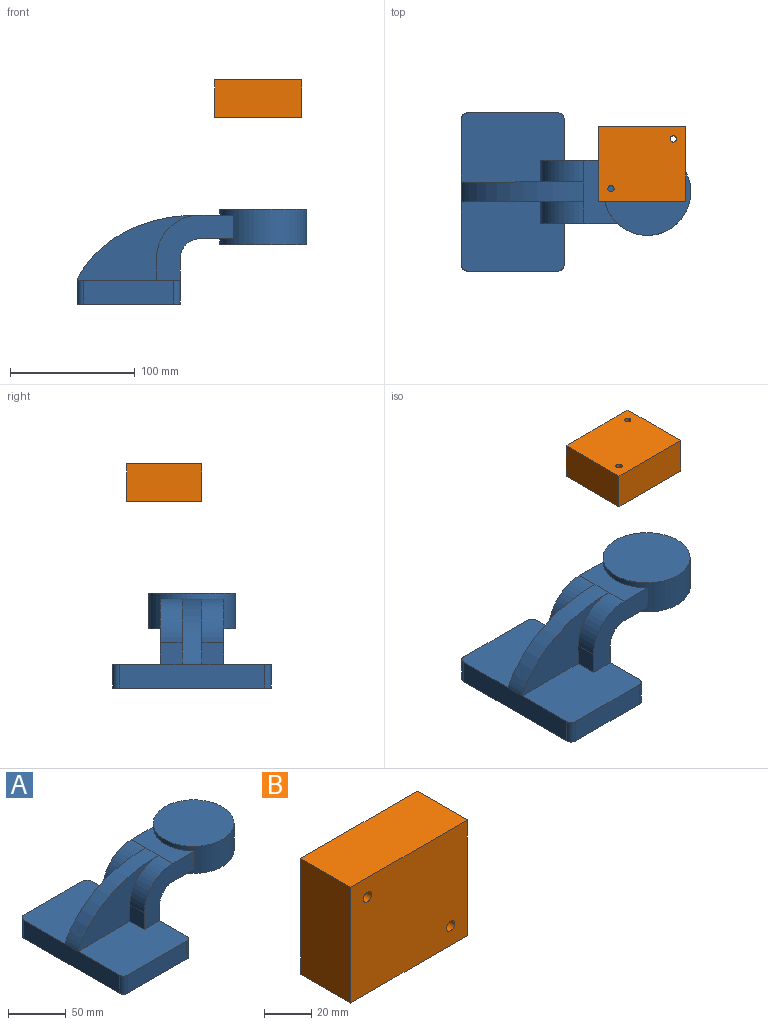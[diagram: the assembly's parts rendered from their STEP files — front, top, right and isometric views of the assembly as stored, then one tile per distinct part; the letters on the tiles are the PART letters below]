
ASSEMBLY  parts=2 mates=1
PART A: 26 faces, bbox 184.2x127x76.2 mm
  f0: plane 61.75x52.4mm, normal (0,-1,0), area 1604.1mm2, adj f5,f8,f11,f12,f13,f14,f15,f19
  f1: plane 61.75x52.4mm, normal (0,1,0), area 1604.1mm2, adj f2,f3,f4,f8,f11,f14,f15,f19
  f2: plane 82.55x55.56mm, normal (0,0,1), area 4242.9mm2, adj f1,f4,f6,f8,f10,f18,f22,f23
  f3: cylinder r=34.92mm len=34.93mm, axis (0,1,0), area 958mm2, adj f1,f4,f11,f18
  f4: plane 17.48x17.46mm, normal (-1,0,0), area 305.2mm2, adj f1,f2,f3,f18
  f5: plane 82.55x55.56mm, normal (0,0,1), area 4242.9mm2, adj f0,f6,f8,f9,f13,f17,f24,f25
  f6: plane 116.84x19.05mm, normal (-1,0,0), area 2225.8mm2, adj f2,f5,f7,f16,f22,f24
  f7: plane 127x82.55mm, normal (0,0,-1), area 10461.7mm2, adj f6,f8,f9,f10,f22,f23,f24,f25
  f8: plane 116.84x36.53mm, normal (1,0,0), area 3113.5mm2, adj f0,f1,f2,f5,f7,f14,f23,f25
  f9: plane 72.39x19.05mm, normal (0,-1,0), area 1379mm2, adj f5,f7,f24,f25
  f10: plane 72.39x19.05mm, normal (0,1,0), area 1379mm2, adj f2,f7,f22,f23
  f11: plane 50.8x26.83mm, normal (0,0,1), area 978.5mm2, adj f0,f1,f3,f12,f16,f19
  f12: cylinder r=34.92mm len=34.93mm, axis (0,1,0), area 958mm2, adj f0,f11,f13,f17
  f13: plane 17.48x17.46mm, normal (-1,0,0), area 305.2mm2, adj f0,f5,f12,f17
  f14: cylinder r=15.88mm len=50.8mm, axis (0,1,0), area 1266.8mm2, adj f0,f1,f8,f15
  f15: plane 50.8x26.83mm, normal (0,0,-1), area 978.5mm2, adj f0,f1,f14,f19
  f16: extruded ~98.43x52.4mm, area 1872.6mm2, adj f6,f11,f17,f18
  f17: plane 98.43x52.43mm, normal (0,-1,0), area 2250.7mm2, adj f5,f12,f13,f16
  f18: plane 98.43x52.43mm, normal (0,1,0), area 2250.7mm2, adj f2,f3,f4,f16
  f19: cylinder r=34.92mm len=69.85mm, axis (0,0,-1), area 5186.9mm2, adj f0,f1,f11,f15,f20,f21
  f20: plane 69.85x69.85mm, normal (0,0,-1), area 3832mm2, adj f19
  f21: plane 69.85x69.85mm, normal (0,0,1), area 3832mm2, adj f19
  f22: cylinder r=5.08mm len=19.05mm, axis (0,0,-1), area 152mm2, adj f2,f6,f7,f10
  f23: cylinder r=5.08mm len=19.05mm, axis (0,0,1), area 152mm2, adj f2,f7,f8,f10
  f24: cylinder r=5.08mm len=19.05mm, axis (0,0,1), area 152mm2, adj f5,f6,f7,f9
  f25: cylinder r=5.08mm len=19.05mm, axis (0,0,-1), area 152mm2, adj f5,f7,f8,f9
PART B: 8 faces, bbox 70x30x60 mm
  f0: plane 70x30mm, normal (0,0,1), area 2100mm2, adj f1,f3,f4,f5
  f1: plane 60x30mm, normal (-1,0,0), area 1800mm2, adj f0,f2,f4,f5
  f2: plane 70x30mm, normal (0,0,-1), area 2100mm2, adj f1,f3,f4,f5
  f3: plane 60x30mm, normal (1,0,0), area 1800mm2, adj f0,f2,f4,f5
  f4: plane 70x60mm, normal (0,-1,0), area 4160.7mm2, adj f0,f1,f2,f3,f6,f7
  f5: plane 70x60mm, normal (0,1,0), area 4160.7mm2, adj f0,f1,f2,f3,f6,f7
  f6: cylinder r=2.5mm len=30mm, axis (0,-1,0), area 471.2mm2, adj f4,f5
  f7: cylinder r=2.5mm len=30mm, axis (0,-1,0), area 471.2mm2, adj f4,f5
PLACE A t=(-50.82,12.29,-10.12)mm fixed
PLACE B rot(axis=(1,0,0),90deg) t=(53.01,34.56,160.26)mm
MATE parallel A.f19 <-> B.f5  axis (0,0,1) through (57.13,12.29,56.56)mm
